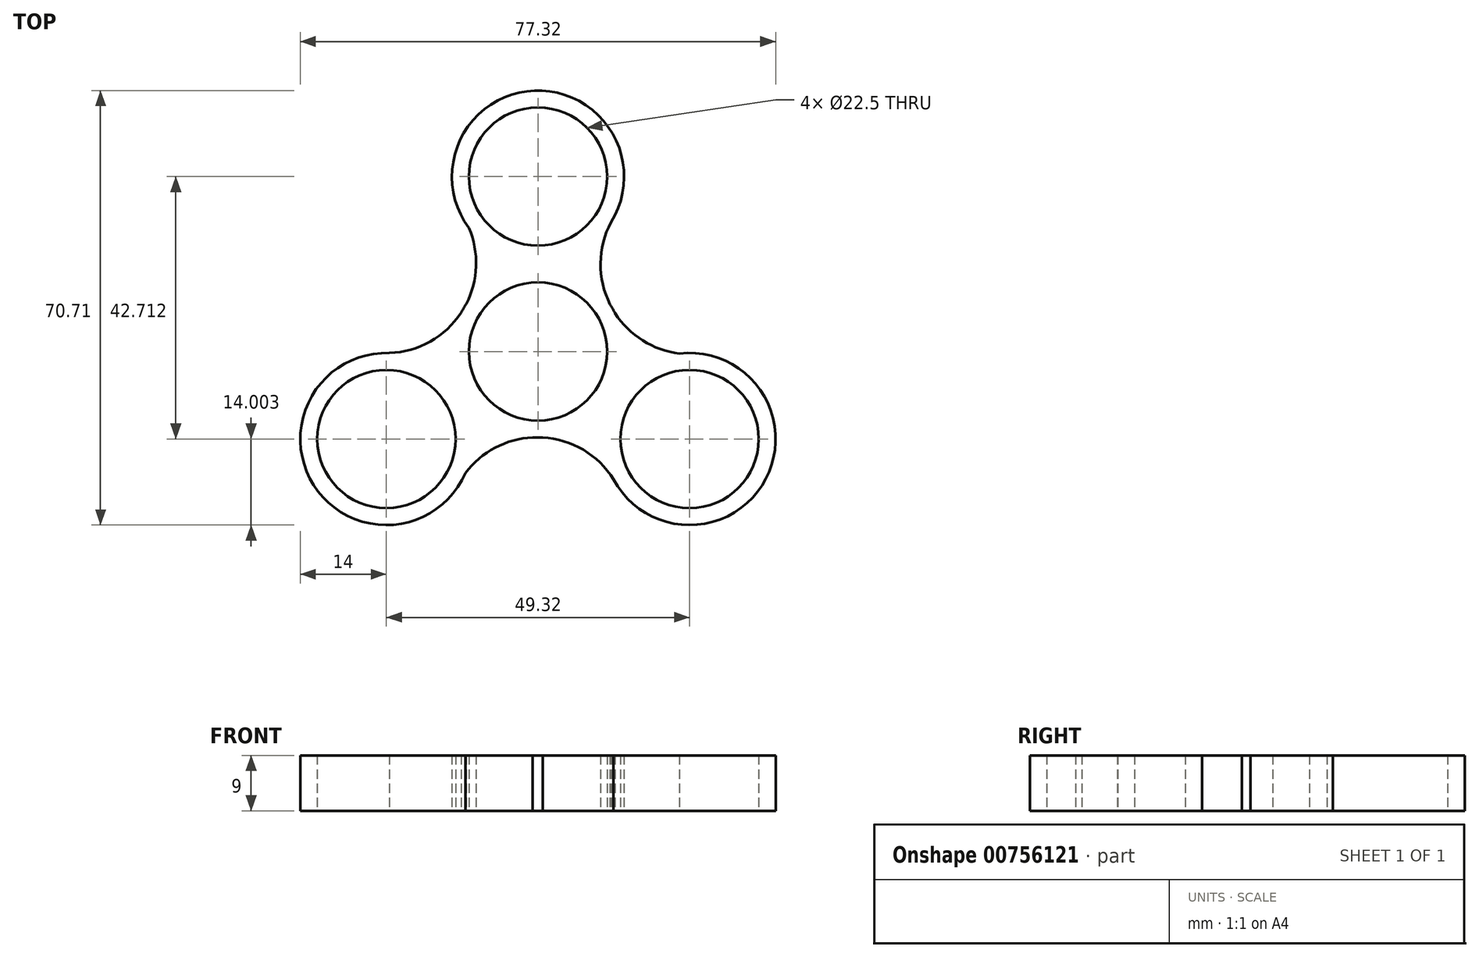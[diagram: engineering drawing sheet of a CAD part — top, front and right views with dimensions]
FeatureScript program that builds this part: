
annotation { "Feature Type Name" : "Feature", "Feature Type Description" : "" }
export const myFeature = defineFeature(function(context is Context, id is Id, definition is map)
    precondition{}
    {
        {
            var Q0;
            Q0=qCreatedBy(makeId("Top.planeOp"),FACE);
            var sketch = newSketch(context, id + "F0", { "sketchPlane" : qUnion([Q0])});
            skCircle(sketch, "E0", {"center": v(0, 0) * mm, "radius": 11.25 * mm});
            skCircle(sketch, "E1", {"center": v(0, 0) * mm, "radius": 14 * mm});
            skCircle(sketch, "E2", {"center": v(0, 28.47) * mm, "radius": 11.25 * mm});
            skCircle(sketch, "E3", {"center": v(0, 28.47) * mm, "radius": 14 * mm});
            skCircle(sketch, "E4.1.0", {"center": v(-24.66, -14.24) * mm, "radius": 11.25 * mm});
            skCircle(sketch, "E4.1.1", {"center": v(-24.66, -14.24) * mm, "radius": 14 * mm});
            skCircle(sketch, "E4.2.0", {"center": v(24.66, -14.24) * mm, "radius": 11.25 * mm});
            skCircle(sketch, "E4.2.1", {"center": v(24.66, -14.24) * mm, "radius": 14 * mm});
            skPoint(sketch, "E5.start.orphan", {"position": v(29.67, 0) * mm});
            skArc(sketch, "E6", {"start": v(12.4, 21.97) * mm, "mid": v(11.6, 7.9) * mm, "end": v(23.02, -0.33) * mm});
            skArc(sketch, "E7.1.0", {"start": v(-25.22, -0.25) * mm, "mid": v(-12.65, 6.1) * mm, "end": v(-11.22, 20.1) * mm});
            skArc(sketch, "E7.2.0", {"start": v(12.83, -21.72) * mm, "mid": v(1.05, -14) * mm, "end": v(-11.8, -19.77) * mm});
            skSolve(sketch);
        }
        {
            var Q0;
            Q0 = qSketchRegion(id + "F0", true);
            extrude(context, id + "F1", {"entities" : qUnion([Q0]), "depth" : 9 * mm, "offsetDistance" : 25 * mm});
        }
    });
